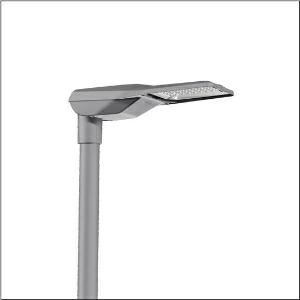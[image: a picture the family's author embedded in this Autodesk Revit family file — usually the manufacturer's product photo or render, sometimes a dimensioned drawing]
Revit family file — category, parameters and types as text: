
# Revit family: streetlight_sl_21_iq_mini___st1_0a_5xe2d41d08jb_acb7
name_source: partatom
category: Lighting Fixtures
units: mm (PartAtom-declared; Revit-internal decimal feet)

## family parameters
Cut with Voids When Loaded = No
Host = Face
Light Source = No
Part Type = Normal
Room Calculation Point = No
Round Connector Dimension = Use Diameter
Shared = No

## types (1)
- --- (1 x LED, 11290 lm, 71.6 W, 4000K)
    Apparent Load = 72 VA
    CIE Flux Codes = 40 73 97 100 100
    Color Rendering = 70
    Color Temperature = 4000K
    Default Elevation = 1800 mm
    Description = Streetlight SL 21 iQ mini, mast luminaire, primary light control with lens, of PMMA, primary optical cover: cover, of toughened safety glass, transparent, light distribution: ST1.0a, light emission: direct distribution, primary light characteristic: asymmetric, installation type: post-top, side-entry, LED, High Power LED, rated luminous flux: 11.290lm, luminous efficacy: 158lm/W, light colour: 740, colour temperature: 4000K, control: Auto-Match, Temp-Guard, Lumen-Switch, Night-Set, Smart-Wire, Light-Fading, Desk-Remote (wireless, voltage-free reading and setting of iQ features in the workshop via application-optimized NFC function/RFID function), optimised constant luminous flux control (CLO 2.0), presetting dimming linear, mains connection: 220..240V, AC, 50/60Hz, start of lifetime: 72W, end of service life: 75W, reduction: 33W, luminaire housing, of diecast aluminium, powder-coated, Siteco® metallic grey (DB 702S), corrosivity category C5 mid according to DIN EN ISO 12944, please order mast flange separately, inclination adjustable: 0°, 5°, 10°, 15°, sealing non-destructively replaceable, multi-level sealing system, length: 628mm, width: 235mm, height: 110mm, mast flange for spigot size: 42mm (side-entry): 5XC10008XM4, 60/48mm (side-entry/post-top): 5XC10108XM2, 76/60mm (side-entry/post-top): 5XC10108XM1, protection rating (complete): IP66, insulation class (complete): insulation class II (safety insulation), certification: CE, ENEC, ENEC+, VDE, impact resistance: IK09, permissible operating ambient temperature for outdoor applications: -40..+50°C, standard-compliant lighting for roads and squares, packaging unit: 1 piece

Light Distribution: ST1.0a
    Height = 110 mm
    Lamp = 1 x LED
    Lamp Light Flux = 11290 lm
    Lamp Power = 71.6 W
    Lamp count = 1
    Length = 625 mm
    Luminous efficacy = 158 lm/W
    Manufacturer = Siteco
    ModVariant = No
    Model = 5XE2D41D08JB
    Number of Poles = 1
    OnlyDefault = Yes
    Power Factor = 1
    Product Name = Streetlight SL 21 iQ mini | ST1.0a
    Product group = mast luminaire | pylon top
    ProductGroupID = 6100
    Protection Class = Protection class II
    Protection Degree = IP 66
    RLX_Detail_Level = 1
    RLX_Emergency_Light_Flux = 0 lm
    RLX_Emergency_Type = 0
    RLX_Emergency_Type_DB = No
    RlxData = <blob elided: 92005 chars, md5=b10eb9f3>
    Socket = socket
    Standby Power = 0 W
    System Light Flux = 11290 lm
    System Power = 72 W
    Type Comments = factory setting: luminous flux: 100 % | dim-lin: 254 | 746 mA
    Type Image = l_1003519.jpg
    URL = http://relux.com
    VarID = @adj_104047
    Voltage = 0 V
    Weight = 0.00 kg
    Width = 234 mm

## geometry (parser evidence)
native form markers: Blend x4, Sweep x9
no freeform markers — native parametric forms only
